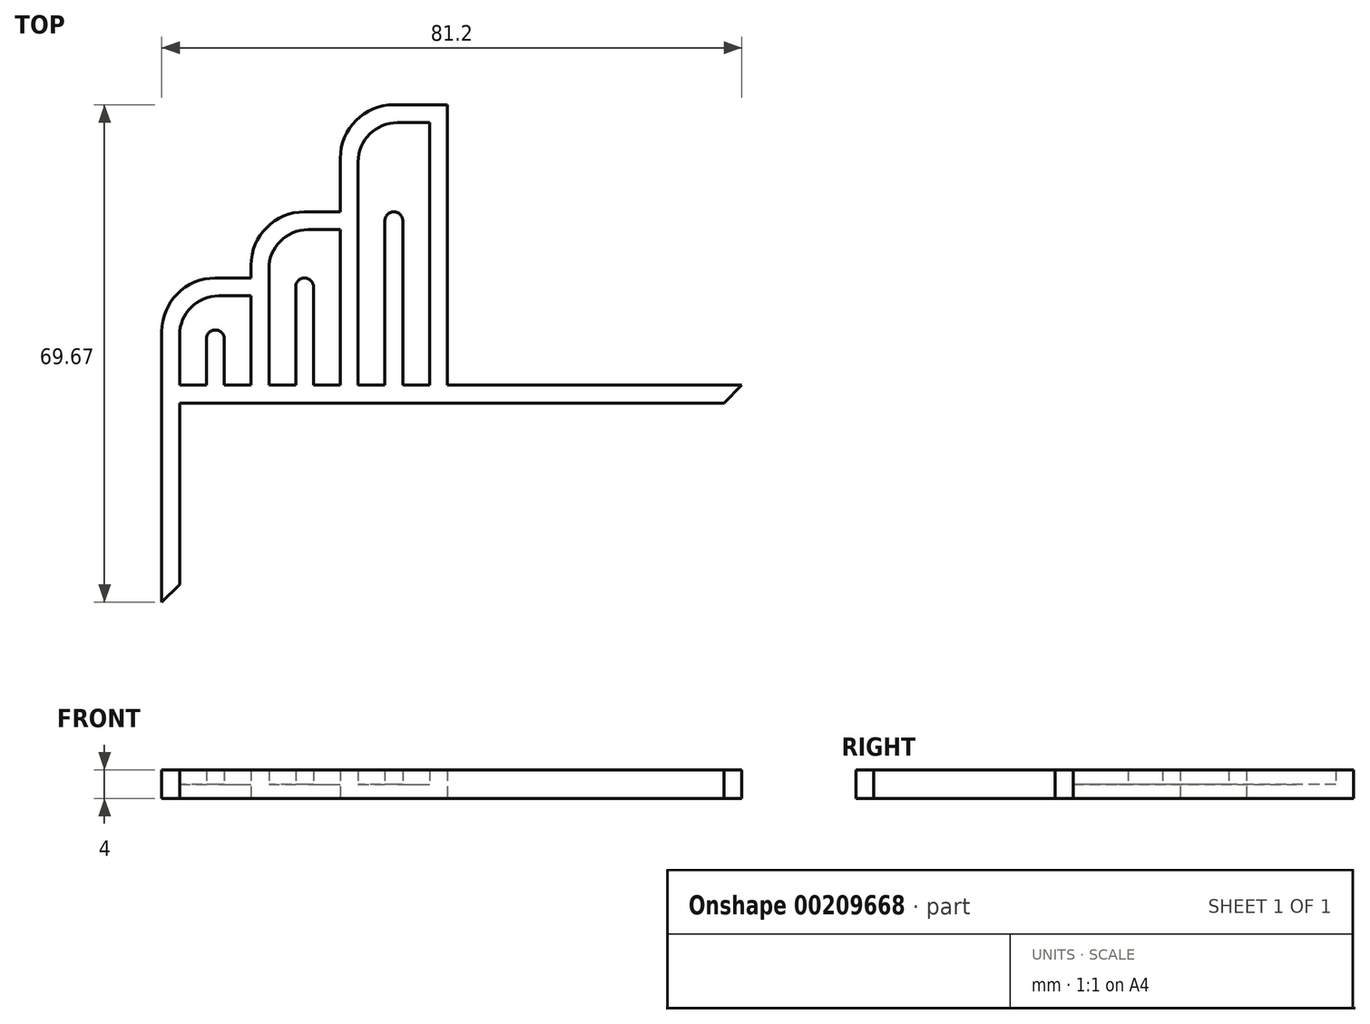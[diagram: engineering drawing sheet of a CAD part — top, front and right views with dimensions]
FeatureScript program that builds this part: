
annotation { "Feature Type Name" : "Feature", "Feature Type Description" : "" }
export const myFeature = defineFeature(function(context is Context, id is Id, definition is map)
    precondition{}
    {
        {
            var Q0;
            Q0=qCreatedBy(makeId("Top.planeOp"),FACE);
            var sketch = newSketch(context, id + "F0", { "sketchPlane" : qUnion([Q0])});
            skLineSegment(sketch, "E0", {"start": v(0, 0) * mm, "end": v(0, 25.4) * mm});
            skLineSegment(sketch, "E1", {"start": v(0, 25.4) * mm, "end": v(76.2, 25.4) * mm});
            skLineSegment(sketch, "E2", {"start": v(76.2, 25.4) * mm, "end": v(78.7, 27.9) * mm});
            skLineSegment(sketch, "E3", {"start": v(78.7, 27.9) * mm, "end": v(37.5, 27.9) * mm});
            skLineSegment(sketch, "E4", {"start": v(-2.5, 27.9) * mm, "end": v(-2.5, -2.5) * mm});
            skLineSegment(sketch, "E5", {"start": v(-2.5, -2.5) * mm, "end": v(0, 0) * mm});
            skLineSegment(sketch, "E6", {"start": v(-2.5, 27.9) * mm, "end": v(-2.5, 35.4) * mm});
            skLineSegment(sketch, "E7", {"start": v(5, 42.9) * mm, "end": v(10, 42.9) * mm});
            skLineSegment(sketch, "E8", {"start": v(10, 40.4) * mm, "end": v(10, 27.9) * mm});
            skLineSegment(sketch, "E9", {"start": v(10, 42.9) * mm, "end": v(10, 44.67) * mm});
            skLineSegment(sketch, "E10", {"start": v(17.5, 52.17) * mm, "end": v(22.5, 52.17) * mm});
            skLineSegment(sketch, "E11", {"start": v(22.5, 49.67) * mm, "end": v(22.5, 27.9) * mm});
            skLineSegment(sketch, "E12", {"start": v(22.5, 52.17) * mm, "end": v(22.5, 59.67) * mm});
            skLineSegment(sketch, "E13", {"start": v(30, 67.17) * mm, "end": v(35, 67.17) * mm});
            skLineSegment(sketch, "E14", {"start": v(35, 64.67) * mm, "end": v(35, 27.9) * mm});
            skPoint(sketch, "E15.visualSharp", {"position": v(-2.5, 42.9) * mm});
            skArc(sketch, "E15.filletArc", {"start": v(5, 42.9) * mm, "mid": v(-0.3, 40.7) * mm, "end": v(-2.5, 35.4) * mm});
            skPoint(sketch, "E16.visualSharp", {"position": v(10, 52.17) * mm});
            skArc(sketch, "E16.filletArc", {"start": v(17.5, 52.17) * mm, "mid": v(12.2, 49.97) * mm, "end": v(10, 44.67) * mm});
            skPoint(sketch, "E17.visualSharp", {"position": v(22.5, 67.17) * mm});
            skArc(sketch, "E17.filletArc", {"start": v(30, 67.17) * mm, "mid": v(24.7, 64.97) * mm, "end": v(22.5, 59.67) * mm});
            skLineSegment(sketch, "E18", {"start": v(0, 27.9) * mm, "end": v(0, 34.9) * mm});
            skLineSegment(sketch, "E19", {"start": v(0, 27.9) * mm, "end": v(10, 27.9) * mm});
            skLineSegment(sketch, "E20", {"start": v(5.5, 40.4) * mm, "end": v(10, 40.4) * mm});
            skPoint(sketch, "E21.newPointA", {"position": v(0, 35.4) * mm});
            skPoint(sketch, "E21.newPointB", {"position": v(5, 40.4) * mm});
            skArc(sketch, "E21.filletArc", {"start": v(5.5, 40.4) * mm, "mid": v(1.61, 38.79) * mm, "end": v(0, 34.9) * mm});
            skLineSegment(sketch, "E22", {"start": v(12.5, 27.9) * mm, "end": v(22.5, 27.9) * mm});
            skLineSegment(sketch, "E23", {"start": v(12.5, 27.9) * mm, "end": v(12.5, 44.17) * mm});
            skLineSegment(sketch, "E24", {"start": v(18, 49.67) * mm, "end": v(22.5, 49.67) * mm});
            skPoint(sketch, "E25.orphan", {"position": v(12.5, 44.67) * mm});
            skPoint(sketch, "E26.visualSharp", {"position": v(12.5, 49.67) * mm});
            skArc(sketch, "E26.filletArc", {"start": v(18, 49.67) * mm, "mid": v(14.11, 48.06) * mm, "end": v(12.5, 44.17) * mm});
            skLineSegment(sketch, "E27", {"start": v(25, 27.9) * mm, "end": v(25, 59.17) * mm});
            skLineSegment(sketch, "E28", {"start": v(30.5, 64.67) * mm, "end": v(35, 64.67) * mm});
            skPoint(sketch, "E29.visualSharp", {"position": v(25, 64.67) * mm});
            skArc(sketch, "E29.filletArc", {"start": v(30.5, 64.67) * mm, "mid": v(26.61, 63.06) * mm, "end": v(25, 59.17) * mm});
            skLineSegment(sketch, "E30", {"start": v(35, 67.17) * mm, "end": v(37.5, 67.17) * mm});
            skLineSegment(sketch, "E31", {"start": v(37.5, 67.17) * mm, "end": v(37.5, 27.9) * mm});
            skLineSegment(sketch, "E32", {"start": v(25, 27.9) * mm, "end": v(35, 27.9) * mm});
            skSolve(sketch);
        }
        {
            var Q0;
            Q0=makeQuery(id+"F0.imprint","IMPRINT",FACE,{"disambiguationData":[TD([[makeQuery(id+"F0.imprint","IMPRINT",EDGE,{"derivedFrom":sQuery(id+"F0.wireOp",EDGE,"E0")}),1.0]])]});
            extrude(context, id + "F1", {"entities" : qUnion([Q0]), "depth" : 2 * mm});
        }
        {
            var Q0;
            Q0=makeQuery(id+"F1.opExtrude","CAP_FACE",FACE,{"disambiguationData":[OSD([sQuery(id+"F0.wireOp",EDGE,"E0"),sQuery(id+"F0.wireOp",EDGE,"E1"),sQuery(id+"F0.wireOp",EDGE,"E2"),sQuery(id+"F0.wireOp",EDGE,"E3"),sQuery(id+"F0.wireOp",EDGE,"E4"),sQuery(id+"F0.wireOp",EDGE,"E5"),sQuery(id+"F0.wireOp",EDGE,"E6"),sQuery(id+"F0.wireOp",EDGE,"E7"),sQuery(id+"F0.wireOp",EDGE,"E8"),sQuery(id+"F0.wireOp",EDGE,"E9"),sQuery(id+"F0.wireOp",EDGE,"E10"),sQuery(id+"F0.wireOp",EDGE,"E11"),sQuery(id+"F0.wireOp",EDGE,"E12"),sQuery(id+"F0.wireOp",EDGE,"E13"),sQuery(id+"F0.wireOp",EDGE,"E14"),sQuery(id+"F0.wireOp",EDGE,"E15.filletArc"),sQuery(id+"F0.wireOp",EDGE,"E16.filletArc"),sQuery(id+"F0.wireOp",EDGE,"E17.filletArc"),sQuery(id+"F0.wireOp",EDGE,"E18"),sQuery(id+"F0.wireOp",EDGE,"E19"),sQuery(id+"F0.wireOp",EDGE,"E20"),sQuery(id+"F0.wireOp",EDGE,"E21.filletArc"),sQuery(id+"F0.wireOp",EDGE,"E22"),sQuery(id+"F0.wireOp",EDGE,"E23"),sQuery(id+"F0.wireOp",EDGE,"E24"),sQuery(id+"F0.wireOp",EDGE,"E26.filletArc"),sQuery(id+"F0.wireOp",EDGE,"E27"),sQuery(id+"F0.wireOp",EDGE,"E28"),sQuery(id+"F0.wireOp",EDGE,"E29.filletArc"),sQuery(id+"F0.wireOp",EDGE,"E30"),sQuery(id+"F0.wireOp",EDGE,"E31"),sQuery(id+"F0.wireOp",EDGE,"E32")])],"isStart":true});
            var sketch = newSketch(context, id + "F2", { "sketchPlane" : qUnion([Q0])});
            skLineSegment(sketch, "E33", {"start": v(-2.5, 2.5) * mm, "end": v(0, 0) * mm});
            skLineSegment(sketch, "E34", {"start": v(0, 0) * mm, "end": v(0, -25.4) * mm});
            skLineSegment(sketch, "E35", {"start": v(0, -25.4) * mm, "end": v(76.2, -25.4) * mm});
            skLineSegment(sketch, "E36", {"start": v(76.2, -25.4) * mm, "end": v(78.7, -27.9) * mm});
            skLineSegment(sketch, "E37", {"start": v(78.7, -27.9) * mm, "end": v(37.5, -27.9) * mm});
            skLineSegment(sketch, "E38", {"start": v(37.5, -27.9) * mm, "end": v(37.5, -67.17) * mm});
            skLineSegment(sketch, "E39", {"start": v(37.5, -67.17) * mm, "end": v(30, -67.17) * mm});
            skLineSegment(sketch, "E40", {"start": v(-2.5, 2.5) * mm, "end": v(-2.5, -35.4) * mm});
            skLineSegment(sketch, "E41", {"start": v(5, -42.9) * mm, "end": v(10, -42.9) * mm});
            skLineSegment(sketch, "E42", {"start": v(10, -42.9) * mm, "end": v(10, -44.67) * mm});
            skLineSegment(sketch, "E43", {"start": v(17.5, -52.17) * mm, "end": v(22.5, -52.17) * mm});
            skLineSegment(sketch, "E44", {"start": v(22.5, -52.17) * mm, "end": v(22.5, -59.67) * mm});
            skArc(sketch, "E45", {"start": v(-2.5, -35.4) * mm, "mid": v(-0.3, -40.7) * mm, "end": v(5, -42.9) * mm});
            skArc(sketch, "E46", {"start": v(10, -44.67) * mm, "mid": v(12.2, -49.97) * mm, "end": v(17.5, -52.17) * mm});
            skArc(sketch, "E47", {"start": v(22.5, -59.67) * mm, "mid": v(24.7, -64.97) * mm, "end": v(30, -67.17) * mm});
            skSolve(sketch);
        }
        {
            var Q0;
            Q0 = qSketchRegion(id + "F2", true);
            extrude(context, id + "F3", {"entities" : qUnion([Q0]), "operationType" : NewBodyOperationType.ADD, "depth" : 2 * mm});
        }
        {
            var Q0;
            Q0=makeQuery(id+"F3.boolean.opBoolean","SPLIT",FACE,{"disambiguationData":[TD([makeQuery(id+"F1.opExtrude","SWEPT_FACE",FACE,{"disambiguationData":[OSD([sQuery(id+"F0.wireOp",EDGE,"E8")])]})])],"derivedFrom":makeQuery(id+"F3.opExtrude","CAP_FACE",FACE,{"disambiguationData":[OSD([sQuery(id+"F2.wireOp",EDGE,"E33"),sQuery(id+"F2.wireOp",EDGE,"E34"),sQuery(id+"F2.wireOp",EDGE,"E35"),sQuery(id+"F2.wireOp",EDGE,"E36"),sQuery(id+"F2.wireOp",EDGE,"E37"),sQuery(id+"F2.wireOp",EDGE,"E38"),sQuery(id+"F2.wireOp",EDGE,"E39"),sQuery(id+"F2.wireOp",EDGE,"E40"),sQuery(id+"F2.wireOp",EDGE,"E41"),sQuery(id+"F2.wireOp",EDGE,"E42"),sQuery(id+"F2.wireOp",EDGE,"E43"),sQuery(id+"F2.wireOp",EDGE,"E44"),sQuery(id+"F2.wireOp",EDGE,"E45"),sQuery(id+"F2.wireOp",EDGE,"E46"),sQuery(id+"F2.wireOp",EDGE,"E47")])],"isStart":true})});
            var sketch = newSketch(context, id + "F4", { "sketchPlane" : qUnion([Q0])});
            skLineSegment(sketch, "E48.bottom", {"start": v(5, 35.63) * mm, "end": v(5, 35.63) * mm});
            skLineSegment(sketch, "E48.top", {"start": v(3.75, 27.9) * mm, "end": v(6.25, 27.9) * mm});
            skLineSegment(sketch, "E48.left", {"start": v(3.75, 34.38) * mm, "end": v(3.75, 27.9) * mm});
            skLineSegment(sketch, "E48.right", {"start": v(6.25, 34.38) * mm, "end": v(6.25, 27.9) * mm});
            skPoint(sketch, "E49.visualSharp", {"position": v(3.75, 35.63) * mm});
            skArc(sketch, "E49.filletArc", {"start": v(5, 35.63) * mm, "mid": v(4.12, 35.26) * mm, "end": v(3.75, 34.38) * mm});
            skPoint(sketch, "E50.visualSharp", {"position": v(6.25, 35.63) * mm});
            skArc(sketch, "E50.filletArc", {"start": v(6.25, 34.38) * mm, "mid": v(5.88, 35.26) * mm, "end": v(5, 35.63) * mm});
            skSolve(sketch);
        }
        {
            var Q0;
            Q0=makeQuery(id+"F4.imprint","IMPRINT",FACE,{"disambiguationData":[TD([[makeQuery(id+"F4.imprint","IMPRINT",EDGE,{"derivedFrom":sQuery(id+"F4.wireOp",EDGE,"E48.top")}),1.0]])]});
            extrude(context, id + "F5", {"entities" : qUnion([Q0]), "operationType" : NewBodyOperationType.ADD, "depth" : 2 * mm});
        }
        {
            var Q0;
            Q0=makeQuery(id+"F3.boolean.opBoolean","SPLIT",FACE,{"disambiguationData":[TD([makeQuery(id+"F1.opExtrude","SWEPT_FACE",FACE,{"disambiguationData":[OSD([sQuery(id+"F0.wireOp",EDGE,"E11")])]})])],"derivedFrom":makeQuery(id+"F3.opExtrude","CAP_FACE",FACE,{"disambiguationData":[OSD([sQuery(id+"F2.wireOp",EDGE,"E33"),sQuery(id+"F2.wireOp",EDGE,"E34"),sQuery(id+"F2.wireOp",EDGE,"E35"),sQuery(id+"F2.wireOp",EDGE,"E36"),sQuery(id+"F2.wireOp",EDGE,"E37"),sQuery(id+"F2.wireOp",EDGE,"E38"),sQuery(id+"F2.wireOp",EDGE,"E39"),sQuery(id+"F2.wireOp",EDGE,"E40"),sQuery(id+"F2.wireOp",EDGE,"E41"),sQuery(id+"F2.wireOp",EDGE,"E42"),sQuery(id+"F2.wireOp",EDGE,"E43"),sQuery(id+"F2.wireOp",EDGE,"E44"),sQuery(id+"F2.wireOp",EDGE,"E45"),sQuery(id+"F2.wireOp",EDGE,"E46"),sQuery(id+"F2.wireOp",EDGE,"E47")])],"isStart":true})});
            var sketch = newSketch(context, id + "F6", { "sketchPlane" : qUnion([Q0])});
            skLineSegment(sketch, "E51.bottom", {"start": v(17.5, 42.9) * mm, "end": v(17.5, 42.9) * mm});
            skLineSegment(sketch, "E51.top", {"start": v(16.25, 27.9) * mm, "end": v(18.75, 27.9) * mm});
            skLineSegment(sketch, "E51.left", {"start": v(16.25, 41.65) * mm, "end": v(16.25, 27.9) * mm});
            skLineSegment(sketch, "E51.right", {"start": v(18.75, 41.65) * mm, "end": v(18.75, 27.9) * mm});
            skPoint(sketch, "E52.visualSharp", {"position": v(16.25, 42.9) * mm});
            skArc(sketch, "E52.filletArc", {"start": v(17.5, 42.9) * mm, "mid": v(16.62, 42.53) * mm, "end": v(16.25, 41.65) * mm});
            skPoint(sketch, "E53.visualSharp", {"position": v(18.75, 42.9) * mm});
            skArc(sketch, "E53.filletArc", {"start": v(18.75, 41.65) * mm, "mid": v(18.38, 42.53) * mm, "end": v(17.5, 42.9) * mm});
            skSolve(sketch);
        }
        {
            var Q0;
            Q0=makeQuery(id+"F6.imprint","IMPRINT",FACE,{"disambiguationData":[TD([[makeQuery(id+"F6.imprint","IMPRINT",EDGE,{"derivedFrom":sQuery(id+"F6.wireOp",EDGE,"E51.top")}),1.0]])]});
            extrude(context, id + "F7", {"entities" : qUnion([Q0]), "operationType" : NewBodyOperationType.ADD, "depth" : 2 * mm});
        }
        {
            var Q0;
            Q0=makeQuery(id+"F3.boolean.opBoolean","SPLIT",FACE,{"disambiguationData":[TD([makeQuery(id+"F1.opExtrude","SWEPT_FACE",FACE,{"disambiguationData":[OSD([sQuery(id+"F0.wireOp",EDGE,"E14")])]})])],"derivedFrom":makeQuery(id+"F3.opExtrude","CAP_FACE",FACE,{"disambiguationData":[OSD([sQuery(id+"F2.wireOp",EDGE,"E33"),sQuery(id+"F2.wireOp",EDGE,"E34"),sQuery(id+"F2.wireOp",EDGE,"E35"),sQuery(id+"F2.wireOp",EDGE,"E36"),sQuery(id+"F2.wireOp",EDGE,"E37"),sQuery(id+"F2.wireOp",EDGE,"E38"),sQuery(id+"F2.wireOp",EDGE,"E39"),sQuery(id+"F2.wireOp",EDGE,"E40"),sQuery(id+"F2.wireOp",EDGE,"E41"),sQuery(id+"F2.wireOp",EDGE,"E42"),sQuery(id+"F2.wireOp",EDGE,"E43"),sQuery(id+"F2.wireOp",EDGE,"E44"),sQuery(id+"F2.wireOp",EDGE,"E45"),sQuery(id+"F2.wireOp",EDGE,"E46"),sQuery(id+"F2.wireOp",EDGE,"E47")])],"isStart":true})});
            var sketch = newSketch(context, id + "F8", { "sketchPlane" : qUnion([Q0])});
            skLineSegment(sketch, "E54.bottom", {"start": v(30, 52.17) * mm, "end": v(30, 52.17) * mm});
            skLineSegment(sketch, "E54.top", {"start": v(28.75, 27.9) * mm, "end": v(31.25, 27.9) * mm});
            skLineSegment(sketch, "E54.left", {"start": v(28.75, 50.92) * mm, "end": v(28.75, 27.9) * mm});
            skLineSegment(sketch, "E54.right", {"start": v(31.25, 50.92) * mm, "end": v(31.25, 27.9) * mm});
            skPoint(sketch, "E55.visualSharp", {"position": v(28.75, 52.17) * mm});
            skArc(sketch, "E55.filletArc", {"start": v(30, 52.17) * mm, "mid": v(29.12, 51.8) * mm, "end": v(28.75, 50.92) * mm});
            skPoint(sketch, "E56.visualSharp", {"position": v(31.25, 52.17) * mm});
            skArc(sketch, "E56.filletArc", {"start": v(31.25, 50.92) * mm, "mid": v(30.88, 51.8) * mm, "end": v(30, 52.17) * mm});
            skSolve(sketch);
        }
        {
            var Q0;
            Q0=makeQuery(id+"F8.imprint","IMPRINT",FACE,{"disambiguationData":[TD([[makeQuery(id+"F8.imprint","IMPRINT",EDGE,{"derivedFrom":sQuery(id+"F8.wireOp",EDGE,"E54.top")}),1.0]])]});
            extrude(context, id + "F9", {"entities" : qUnion([Q0]), "operationType" : NewBodyOperationType.ADD, "depth" : 2 * mm});
        }
    });
